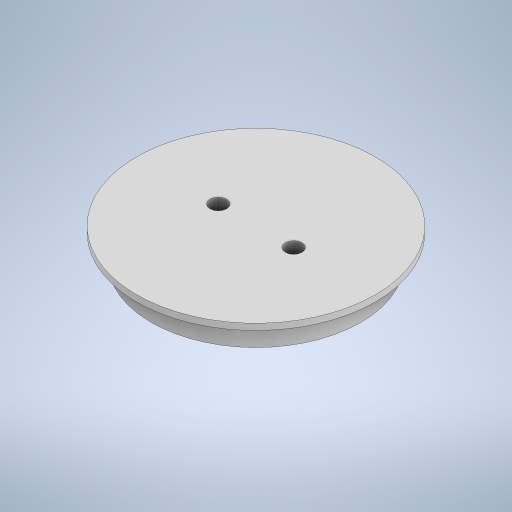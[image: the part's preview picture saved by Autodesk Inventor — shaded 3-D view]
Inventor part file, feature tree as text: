
AUTODESK INVENTOR PART (.ipt)
format: ipt  version: 2023 (Build 270158000, 158)  size: 263,680 bytes
history: native  units: in
note: dims shown in document units (in); Inventor stores cm internally (conversion verified against a paired STEP export)
features: extrude x4, sketch x4, other x2, plane x1
ambient origin geometry x8: Origin, YZ Plane, XZ Plane, XY Plane, X Axis, Y Axis, Z Axis, Center Point
bodies: Solid1 (feature_tree)
feature tree (11):
  extrude  "Extrusion1"  Depth=0.3543in
  extrude  "Extrusion2"  Depth=0.1575in
  extrude  "Extrusion4"  Depth=0.1969in TaperAngle=0.0deg
  plane  "Work Plane1"
  extrude  "Extrusion5"  Depth=0.0591in TaperAngle=0.0deg
  sketch  "Sketch1"  dims[d0=1.063in d1=0.3543in]
  sketch  "Sketch2"  dims[d2=0.3543in d3=0.1575in]
  sketch  "Sketch3"  dims[d4=0.1575in d5=0.1969in d6=0.0in]
  other  "Work Axis3"
  other  "Work Axis4"
  sketch  "Sketch4"  dims[d7=1.9685in d8=0.2362in d9=0.0in d10=2.2441in d13=0.0591in d14=0.0in d15=0.1181in d16=0.0591in d17=0.0in]
